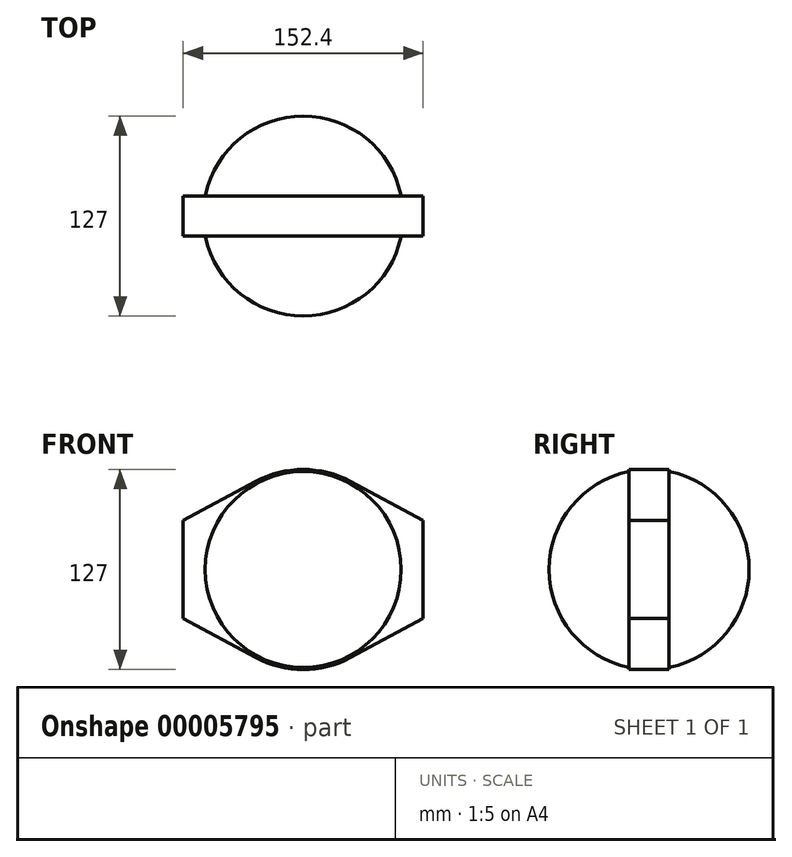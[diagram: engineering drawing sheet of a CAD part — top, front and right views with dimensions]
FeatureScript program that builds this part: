
annotation { "Feature Type Name" : "Feature", "Feature Type Description" : "" }
export const myFeature = defineFeature(function(context is Context, id is Id, definition is map)
    precondition{}
    {
        {
            var Q0;
            Q0=qCreatedBy(makeId("Top.planeOp"),FACE);
            var sketch = newSketch(context, id + "F0", { "sketchPlane" : qUnion([Q0])});
            skLineSegment(sketch, "E0.rect.bottom", {"start": v(63.5, 63.5) * mm, "end": v(-63.5, 63.5) * mm});
            skLineSegment(sketch, "E0.rect.top", {"start": v(63.5, -63.5) * mm, "end": v(-63.5, -63.5) * mm});
            skLineSegment(sketch, "E0.rect.left", {"start": v(63.5, 63.5) * mm, "end": v(63.5, -63.5) * mm});
            skLineSegment(sketch, "E0.rect.right", {"start": v(-63.5, 63.5) * mm, "end": v(-63.5, -63.5) * mm});
            skPoint(sketch, "E0.rect.middle", {"position": v(0, 0) * mm});
            skSolve(sketch);
        }
        {
            var Q0;
            Q0=makeQuery(id+"F0.imprint","IMPRINT",FACE,{"disambiguationData":[TD([[makeQuery(id+"F0.imprint","IMPRINT",EDGE,{"derivedFrom":sQuery(id+"F0.wireOp",EDGE,"E0.rect.bottom")}),1.0]])]});
            extrude(context, id + "F1", {"entities" : qUnion([Q0]), "depth" : 127 * mm});
        }
        {
            var Q0;
            Q0=qCreatedBy(makeId("Front.planeOp"),FACE);
            var sketch = newSketch(context, id + "F2", { "sketchPlane" : qUnion([Q0])});
            skLineSegment(sketch, "E1", {"start": v(63.5, 63.5) * mm, "end": v(-63.5, 63.5) * mm});
            skCircle(sketch, "E2", {"center": v(0, 63.5) * mm, "radius": 63.5 * mm});
            skSolve(sketch);
        }
        {
            var Q0;
            Q0=makeQuery(id+"F1.opExtrude","CAP_EDGE",EDGE,{"disambiguationData":[OSD([sQuery(id+"F0.wireOp",EDGE,"E0.rect.top")])],"isStart":false});
            var Q1;
            Q1=makeQuery(id+"F1.opExtrude","CAP_EDGE",EDGE,{"disambiguationData":[OSD([sQuery(id+"F0.wireOp",EDGE,"E0.rect.left")])],"isStart":false});
            var Q2;
            Q2=makeQuery(id+"F1.opExtrude","CAP_EDGE",EDGE,{"disambiguationData":[OSD([sQuery(id+"F0.wireOp",EDGE,"E0.rect.bottom")])],"isStart":false});
            var Q3;
            Q3=makeQuery(id+"F1.opExtrude","CAP_EDGE",EDGE,{"disambiguationData":[OSD([sQuery(id+"F0.wireOp",EDGE,"E0.rect.right")])],"isStart":false});
            var Q4;
            Q4=makeQuery(id+"F1.opExtrude","SWEPT_EDGE",EDGE,{"disambiguationData":[OSD([sQuery(id+"F0.wireOp",EDGE,"E0.rect.top"),sQuery(id+"F0.wireOp",EDGE,"E0.rect.right")])]});
            var Q5;
            Q5=makeQuery(id+"F1.opExtrude","SWEPT_EDGE",EDGE,{"disambiguationData":[OSD([sQuery(id+"F0.wireOp",EDGE,"E0.rect.top"),sQuery(id+"F0.wireOp",EDGE,"E0.rect.left")])]});
            var Q6;
            Q6=makeQuery(id+"F1.opExtrude","CAP_EDGE",EDGE,{"disambiguationData":[OSD([sQuery(id+"F0.wireOp",EDGE,"E0.rect.top")])],"isStart":true});
            var Q7;
            Q7=makeQuery(id+"F1.opExtrude","SWEPT_EDGE",EDGE,{"disambiguationData":[OSD([sQuery(id+"F0.wireOp",EDGE,"E0.rect.bottom"),sQuery(id+"F0.wireOp",EDGE,"E0.rect.left")])]});
            var Q8;
            Q8=makeQuery(id+"F1.opExtrude","CAP_EDGE",EDGE,{"disambiguationData":[OSD([sQuery(id+"F0.wireOp",EDGE,"E0.rect.left")])],"isStart":true});
            var Q9;
            Q9=makeQuery(id+"F1.opExtrude","CAP_EDGE",EDGE,{"disambiguationData":[OSD([sQuery(id+"F0.wireOp",EDGE,"E0.rect.right")])],"isStart":true});
            var Q10;
            Q10=makeQuery(id+"F1.opExtrude","CAP_EDGE",EDGE,{"disambiguationData":[OSD([sQuery(id+"F0.wireOp",EDGE,"E0.rect.bottom")])],"isStart":true});
            var Q11;
            Q11=makeQuery(id+"F1.opExtrude","SWEPT_EDGE",EDGE,{"disambiguationData":[OSD([sQuery(id+"F0.wireOp",EDGE,"E0.rect.bottom"),sQuery(id+"F0.wireOp",EDGE,"E0.rect.right")])]});
            fillet(context, id + "F3", {"entities" : qUnion([Q0, Q1, Q2, Q3, Q4, Q5, Q6, Q7, Q8, Q9, Q10, Q11]), "radius" : 63.5 * mm, "tangentPropagation" : true, "allowEdgeOverflow" : false});
        }
        {
            var Q0;
            Q0=qCreatedBy(makeId("Front.planeOp"),FACE);
            var sketch = newSketch(context, id + "F4", { "sketchPlane" : qUnion([Q0])});
            skCircle(sketch, "E3.0", {"center": v(0, 63.5) * mm, "radius": 63.5 * mm});
            skLineSegment(sketch, "E4", {"start": v(-76.2, 94.53) * mm, "end": v(-76.2, 32.47) * mm});
            skLineSegment(sketch, "E5", {"start": v(-76.2, 32.47) * mm, "end": v(-30.16, 7.62) * mm});
            skLineSegment(sketch, "E6", {"start": v(-76.2, 94.53) * mm, "end": v(-30.16, 119.38) * mm});
            skLineSegment(sketch, "E7", {"start": v(0, 127) * mm, "end": v(0, 0) * mm, "construction": true});
            skLineSegment(sketch, "E8.0.MirrorCS", {"start": v(76.2, 94.53) * mm, "end": v(30.16, 119.38) * mm});
            skLineSegment(sketch, "E9.0.MirrorCS", {"start": v(76.2, 94.53) * mm, "end": v(76.2, 32.47) * mm});
            skLineSegment(sketch, "E10.0.MirrorCS", {"start": v(76.2, 32.47) * mm, "end": v(30.16, 7.62) * mm});
            skSolve(sketch);
        }
        {
            var Q0;
            Q0 = qSketchRegion(id + "F4", true);
            extrude(context, id + "F5", {"entities" : qUnion([Q0]), "operationType" : NewBodyOperationType.ADD, "endBound" : BoundingType.SYMMETRIC, "depth" : 25.4 * mm});
        }
    });
